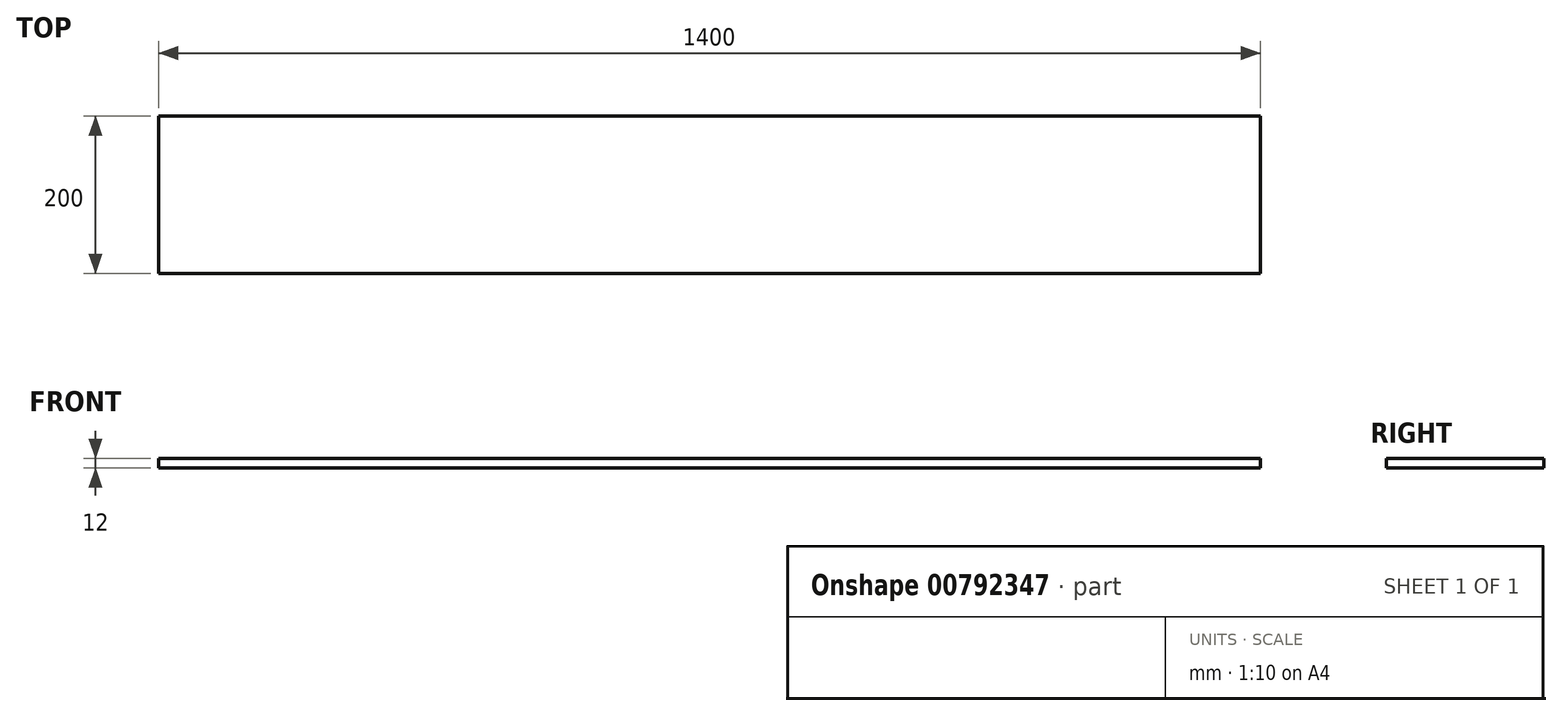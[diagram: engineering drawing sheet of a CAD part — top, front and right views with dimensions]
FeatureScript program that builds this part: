
annotation { "Feature Type Name" : "Feature", "Feature Type Description" : "" }
export const myFeature = defineFeature(function(context is Context, id is Id, definition is map)
    precondition{}
    {
        {
            var Q0;
            Q0=qCreatedBy(makeId("Top.planeOp"),FACE);
            var sketch = newSketch(context, id + "F0", { "sketchPlane" : qUnion([Q0])});
            skLineSegment(sketch, "E0.bottom", {"start": v(-700, 100) * mm, "end": v(700, 100) * mm});
            skLineSegment(sketch, "E0.top", {"start": v(-700, -100) * mm, "end": v(700, -100) * mm});
            skLineSegment(sketch, "E0.left", {"start": v(-700, 100) * mm, "end": v(-700, -100) * mm});
            skLineSegment(sketch, "E0.right", {"start": v(700, 100) * mm, "end": v(700, -100) * mm});
            skLineSegment(sketch, "E1", {"start": v(0, -100) * mm, "end": v(0, 100) * mm, "construction": true});
            skPoint(sketch, "E1.startSnap0", {"position": v(0, -100) * mm});
            skSolve(sketch);
        }
        {
            var Q0;
            Q0 = qSketchRegion(id + "F0", true);
            extrude(context, id + "F1", {"entities" : qUnion([Q0]), "depth" : 12 * mm, "offsetDistance" : 25 * mm});
        }
    });
